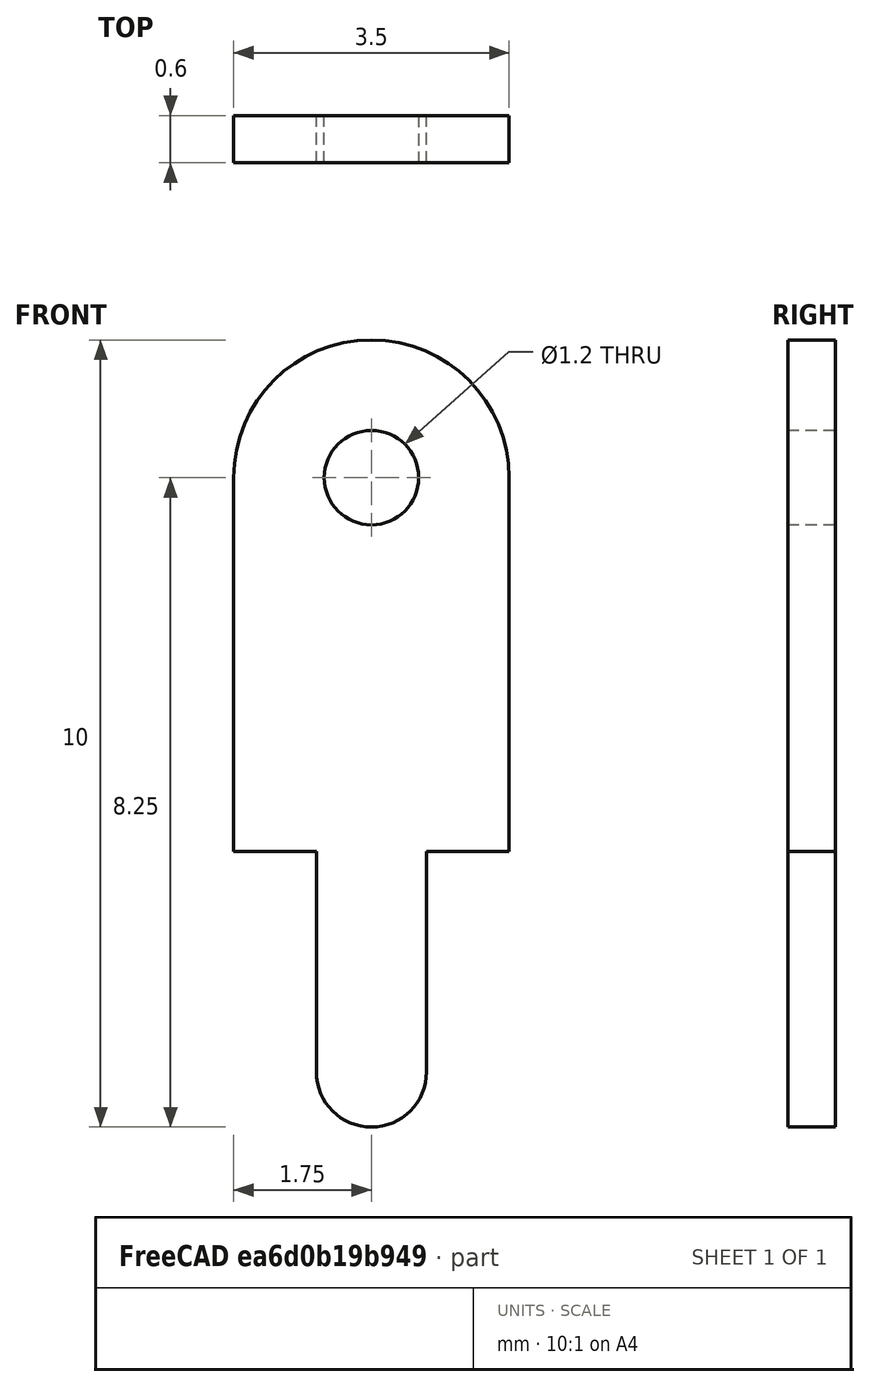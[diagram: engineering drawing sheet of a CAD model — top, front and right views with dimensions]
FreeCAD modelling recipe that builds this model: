
FCSTD DOCUMENT  (FreeCAD 0.17R12018 (Git))
Label: Pin_d1.3mm_L10.0mm_W3.5mm_Flat
License: All rights reserved
LicenseURL: http://en.wikipedia.org/wiki/All_rights_reserved
objects: Spreadsheet::Sheet×1, Sketcher::SketchObject×1, PartDesign::Pad×1, PartDesign::Body×1, App::Part×1
note: 4 computed .brp shape members not serialized (recipe doc carries the construction recipe); baked Part::Feature solids carry a one-line shape summary decoded from their .brp

FEATURE [Spreadsheet::Sheet] Spreadsheet  label="dimensions"
  cells = A1="L"; B1(L)=10; A2="Wtop"; B2(Wtop)=3.5; A3="Wbottom"; B3(Wbottom)=1.3999999999999999; A4="Lbottom"; B4(Lbottom)=3.5; A5="Wfork"; B5(Wfork)=1.2; A7="thick"; B7(thick)=0.59999999999999998
FEATURE [Sketcher::SketchObject] Sketch
  MapMode = 5
  Placement = pos=(0,0,0) rot=(0,0.707107,0.707107;3.14159rad)
  Support = -> [XZ_Plane001]
  expr: Constraints[19] = dimensions.Lbottom - dimensions.Wbottom / 2
  expr: Constraints[21] = (dimensions.Wtop - dimensions.Wbottom) / 2
  expr: Constraints[20] = dimensions.Wbottom
  expr: Constraints[14] = dimensions.L - dimensions.Lbottom - dimensions.Wtop / 2
  expr: Constraints[22] = dimensions.Wtop
  expr: Constraints[25] = dimensions.Wfork / 2
  sketch-geometry (11):
    g0: LineSegment StartX=-1.75 StartY=4.75 StartZ=0 EndX=-1.75 EndY=0 EndZ=0
    g1: LineSegment StartX=-1.75 StartY=0 StartZ=0 EndX=-0.7 EndY=0 EndZ=0
    g2: LineSegment StartX=-0.7 StartY=0 StartZ=0 EndX=-0.7 EndY=-2.8 EndZ=0
    g3: LineSegment StartX=0.7 StartY=0 StartZ=0 EndX=0.7 EndY=-2.8 EndZ=0
    g4: LineSegment StartX=0.7 StartY=0 StartZ=0 EndX=1.75 EndY=0 EndZ=0
    g5: LineSegment StartX=1.75 StartY=0 StartZ=0 EndX=1.75 EndY=4.75 EndZ=0
    g6: ArcOfCircle CenterX=0 CenterY=-2.8 CenterZ=0 NormalX=0 NormalY=0 NormalZ=1 Radius=0.7 StartAngle=3.14159 EndAngle=6.28319
    g7: LineSegment [constr] StartX=-0.7 StartY=-2.8 StartZ=0 EndX=0.7 EndY=-2.8 EndZ=0
    g8: Circle CenterX=0 CenterY=4.75 CenterZ=0 NormalX=0 NormalY=0 NormalZ=1 Radius=0.6
    g9: ArcOfCircle CenterX=0 CenterY=4.75 CenterZ=0 NormalX=0 NormalY=0 NormalZ=1 Radius=1.75 StartAngle=0 EndAngle=3.14159
    g10: LineSegment [constr] StartX=-1.75 StartY=4.75 StartZ=0 EndX=1.75 EndY=4.75 EndZ=0
  constraints (34):
    c: PointOnObject(g3,g-1)
    c: PointOnObject(g6,g-2)
    c: Coincident(g7,g3)
    c: Coincident(g7,g2)
    c: Coincident(g2,g6)
    c: Coincident(g3,g6)
    c: PointOnObject(g6,g7)
    c: Horizontal(g7)
    c: Vertical(g3)
    c: Vertical(g2)
    c: Horizontal(g1)
    c: Horizontal(g4)
    c: Vertical(g5)
    c: Vertical(g0)
    c: DistanceY(g5,g5) = 4.75
    c: Coincident(g5,g4)
    c: Coincident(g0,g1)
    c: Coincident(g4,g3)
    c: Coincident(g1,g2)
    c: DistanceY(g3,g3) = 2.8
    c: DistanceX(g2,g3) = 1.4
    c: DistanceX(g1,g1) = 1.05
    c: DistanceX(g0,g5) = 3.5
    c: PointOnObject(g1,g-1)
    c: PointOnObject(g8,g-2)
    c: Radius(g8) = 0.6
    c: PointOnObject(g9,g-2)
    c: Coincident(g9,g0)
    c: Coincident(g9,g5)
    c: Coincident(g10,g0)
    c: Coincident(g10,g5)
    c: Horizontal(g10)
    c: PointOnObject(g9,g10)
    c: PointOnObject(g8,g10)
FEATURE [PartDesign::Pad] Pad  label="Pin_d1.3mm_L10.0mm_W3.5mm_Flat"
  Length = 0.6
  Length2 = 100
  Midplane = true
  Placement = pos=(0,0,0) rot=(1,0,0;1.5708rad)
  Profile = -> Sketch
  Type = 0
  expr: Length = dimensions.thick
FEATURE [PartDesign::Body] PadBody  label="Body"
  Group = -> [Sketch,Pad]
  Origin = -> Origin001
  Tip = -> Pad
FEATURE [App::Part] Part
  Group = -> [PadBody]
  License = CC BY 3.0
  LicenseURL = http://creativecommons.org/licenses/by/3.0/
  Origin = -> Origin
